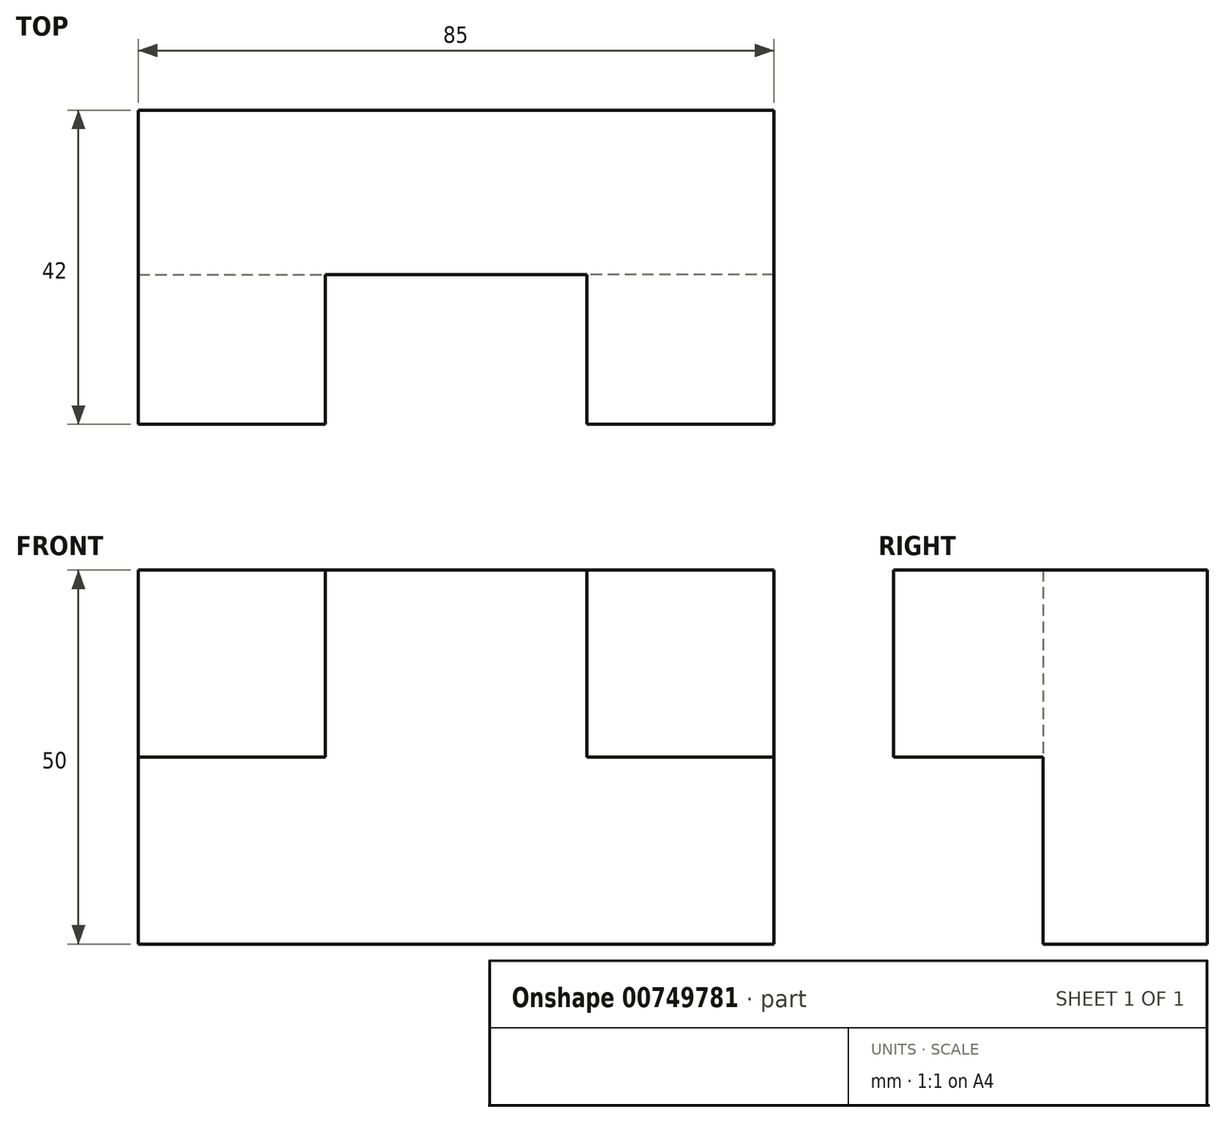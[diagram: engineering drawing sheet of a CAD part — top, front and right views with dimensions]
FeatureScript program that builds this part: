
annotation { "Feature Type Name" : "Feature", "Feature Type Description" : "" }
export const myFeature = defineFeature(function(context is Context, id is Id, definition is map)
    precondition{}
    {
        {
            var Q0;
            Q0=qCreatedBy(makeId("Front.planeOp"),FACE);
            var sketch = newSketch(context, id + "F0", { "sketchPlane" : qUnion([Q0])});
            skLineSegment(sketch, "E0.bottom", {"start": v(0, 0) * mm, "end": v(85, 0) * mm});
            skLineSegment(sketch, "E0.top", {"start": v(0, 50) * mm, "end": v(85, 50) * mm});
            skLineSegment(sketch, "E0.left", {"start": v(0, 0) * mm, "end": v(0, 50) * mm});
            skLineSegment(sketch, "E0.right", {"start": v(85, 0) * mm, "end": v(85, 50) * mm});
            skSolve(sketch);
        }
        {
            var Q0;
            Q0 = qSketchRegion(id + "F0", true);
            extrude(context, id + "F1", {"entities" : qUnion([Q0]), "depth" : 22 * mm, "offsetDistance" : 25 * mm});
        }
        {
            var Q0;
            Q0=makeQuery(id+"F1.opExtrude","CAP_FACE",FACE,{"disambiguationData":[OSD([sQuery(id+"F0.wireOp",EDGE,"E0.bottom"),sQuery(id+"F0.wireOp",EDGE,"E0.top"),sQuery(id+"F0.wireOp",EDGE,"E0.left"),sQuery(id+"F0.wireOp",EDGE,"E0.right")])],"isStart":false});
            var sketch = newSketch(context, id + "F2", { "sketchPlane" : qUnion([Q0])});
            skLineSegment(sketch, "E1.bottom", {"start": v(0, 50) * mm, "end": v(25, 50) * mm});
            skLineSegment(sketch, "E1.top", {"start": v(0, 25) * mm, "end": v(25, 25) * mm});
            skLineSegment(sketch, "E1.left", {"start": v(0, 50) * mm, "end": v(0, 25) * mm});
            skLineSegment(sketch, "E1.right", {"start": v(25, 50) * mm, "end": v(25, 25) * mm});
            skLineSegment(sketch, "E2.bottom", {"start": v(85, 50) * mm, "end": v(60, 50) * mm});
            skLineSegment(sketch, "E2.top", {"start": v(85, 25) * mm, "end": v(60, 25) * mm});
            skLineSegment(sketch, "E2.left", {"start": v(85, 50) * mm, "end": v(85, 25) * mm});
            skLineSegment(sketch, "E2.right", {"start": v(60, 50) * mm, "end": v(60, 25) * mm});
            skSolve(sketch);
        }
        {
            var Q0;
            Q0 = qSketchRegion(id + "F2", true);
            extrude(context, id + "F3", {"entities" : qUnion([Q0]), "operationType" : NewBodyOperationType.ADD, "depth" : 20 * mm, "offsetDistance" : 25 * mm});
        }
    });
